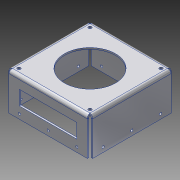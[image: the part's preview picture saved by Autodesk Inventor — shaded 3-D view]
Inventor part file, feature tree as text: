
AUTODESK INVENTOR PART (.ipt)
format: ipt  version: 2015 (Build 190159000, 159)  size: 338,944 bytes
history: native  units: in
note: dims shown in document units (in); Inventor stores cm internally (conversion verified against a paired STEP export)
features: other x6, sketch x5, sheet_metal_op x4, hole x3, projected_geometry x2
ambient origin geometry x8: Origin, YZ Plane, XZ Plane, XY Plane, X Axis, Y Axis, Z Axis, Center Point
bodies: Solid1 (feature_tree)
feature tree (20):
  sketch  "Sketch1"  dims[d4=0.133in d5=0.133in]
  sheet_metal_op  "Face1"
  hole  "Hole1"  [1 undecoded]
  sheet_metal_op  "Flange2"
  other  "A-Side Definition"
  hole  "Hole3"  [1 undecoded]
  hole  "Hole4"  [1 undecoded]
  other  "Plate1"
  sketch  "Sketch3"  dims[d6=0.047in d7=0.047in]
  other  "Plate3"
  sheet_metal_op  "Bend2"
  sheet_metal_op  "Corner2"
  sketch  "Sketch8"  dims[d8=0.133in d9=0.047in]
  sketch  "Sketch9"  dims[d10=2.34in]
  projected_geometry  "Projected Loop9"
  sketch  "Sketch10"  dims[d11=2.34in d12=0.047in d13=0.133in d14=0.047in d15=0.133in d16=6.063in d17=6.063in d18=0.117in d19=0.25in d20=0.25in d21=0.25in d22=0.578in d23=0.25in d24=0.625in d25=0.625in d26=5.68in d27=0.25in d28=5.813in d29=5.813in d30=5.766in d31=0.625in d32=5.813in d33=5.813in d34=0.6915in d35=3.0315in d36=3.0315in d37=3.0315in d38=0.203in d39=5.438in d40=0.25in d41=0.25in d42=0.117in d43=5.813in d44=0.25in d45=0.25in d46=5.391in d47=5.813in d48=5.438in d49=5.438in d50=5.68in d51=5.813in d52=5.813in d53=5.813in d54=4.0in d55=0.125in d56=0.125in d57=0.0in d58=0.25in d59=0.75in d60=0.375in d61=0.25in d62=0.5635in d63=0.125in d64=0.8108in d75=0.125in d76=0.0625in d77=0.25in d78=0.125in d79=2.936in d80=90.0deg d81=0.125in d82=0.5in d83=0.125in d84=0.125in d85=0.3937in d100=0.25in d146=4.5in d147=1.125in d148=0.125in d149=0.0in d150=2.686in d151=0.25in d152=2.936in d153=0.625in d154=0.505in d155=6.1362in d156=0.8181in d157=0.8181in d158=6.1362in d159=0.177in d160=0.177in d161=0.177in d162=0.177in d163=0.75in d164=0.332in d165=0.25in d166=0.5635in d167=0.125in d168=0.8108in d169=0.625in d170=0.505in d171=1.636in d172=1.636in d173=6.1362in d174=6.1362in d175=0.177in d176=0.177in d177=0.177in d178=0.177in d179=0.75in d180=0.332in d181=0.25in d182=0.5635in d183=0.125in d184=0.8108in d185=0.8181in]
  projected_geometry  "Projected Loop10"
  other  "Cut1"
  other  "Cut2"
  other  "Definition1"
note: 3 required parameter values undecoded (feature->parameter linkage not recoverable at this tier; creation-order binding heuristic only, values carry confidence <= 0.55)
